# Revit family: RN 57037 Optifitt-Press-Übergang
name_source: partatom
category: Rohrformteile
units: mm (PartAtom-declared; Revit-internal decimal feet)

## family parameters
Arbeitsebenenbasiert = Nein
Beim Laden mit Abzugskörper schneiden = Nein
Bemaßung runder Anschluss = Durchmesser verwenden
Gemeinsam genutzt = Nein
Immer vertikal = Ja
Teiletyp = Verbindung

## types (9) — shared parameters
1.010.00.2 Blattnummer der Richtlinie = 29
1.010.00.3 Ausgabedatum (Monat) der Richtlinie = 201308
1.010.00.4 Herstellername = R. Nussbaum AG
1.010.00.5 Revisionsdatum der Datei = 20190521
1.010.00.6 Webadresse des Herstellers = http://www.nussbaum.ch
1.100.00.4 Produktbezeichnung = Versorgung
1.110.00.2 Index = 2
1.110.00.4 Produktbezeichnung = Optifitt-Press
1.960/3L.00.8 Link (URL) = https://www.nussbaum.ch
29.700.00.4 Produktname = Optifitt-Press-Übergang, auf Optipress-Therm
29.700.00.5 Produktkennung = 2
29.700.00.6 Querschnittsform = 1
29.700.00.7 Nennweitensystem = DN
29.700.00.8 Nenndrucksystem = PN
29.710.02.4 Nenndruck = 16
29.710.02.5 max. zul. Überdruck [hPa] = 1600
29.710.02.7 max. zul. Dauer-Betriebsdruck [hPa] = 1600
29.710.02.9 max. zul. Dauer-Betriebstemperatur [°C] = 95
Beschreibung = Optifitt-Press-Übergang
Connector Visibility = Nein
EnclosingSpace Visibility = Nein
Hersteller = R. Nussbaum AG
URL = https://www.nussbaum.ch

## per-type parameters (varying)
- DN=25: 1.800.00.3 TGA-Nummer=01900200000000000000000000000000000000000000000016000000000000000009; 1.800.00.4 Kommentarfeld=57037.30, Optifitt-Press-Übergang, auf Optipress-Therm, DN=25, L=79; 1.810.00.3 Hersteller-Bestellnummer=57037.30; 1.810.00.4 DATANORM-Nummer=57037.30; 1.810.00.6 GTIN-Nummer=7612945735096; 29.710.02.10 Formstück-Gewicht [kg]=0.175; 29.710.02.3 Benennung=Optifitt-Press-Übergang, auf Optipress-Therm, DN=25, L=79; CONNECTOR0_DIAMETER_dX_0r=25 mm  [stored 0.082021 ft]; CONNECTOR0_dX_01=34 mm; CONNECTOR0_ref_dX=34 mm; CONNECTOR1_DIAMETER_dX_0r=25 mm  [stored 0.082021 ft]; CONNECTOR1_dX_00=57 mm; CONNECTOR1_dX_01=79 mm; CONNECTOR1_ref_dX=57 mm; Modell=57037.3; R. Nussbaum AG 57037.22 de Visibility=Nein; R. Nussbaum AG 57037.23 de Visibility=Nein; R. Nussbaum AG 57037.24 de Visibility=Nein; R. Nussbaum AG 57037.25 de Visibility=Nein; R. Nussbaum AG 57037.26 de Visibility=Nein; R. Nussbaum AG 57037.27 de Visibility=Nein; R. Nussbaum AG 57037.28 de Visibility=Nein; R. Nussbaum AG 57037.29 de Visibility=Nein; R. Nussbaum AG 57037.30 de Visibility=Ja; Typenkommentare=Optifitt-Press-Übergang  DN=25
- DN=20: 1.800.00.3 TGA-Nummer=01900200000000000000000000000000000000000000000016000000000000000008; 1.800.00.4 Kommentarfeld=57037.29, Optifitt-Press-Übergang, auf Optipress-Therm, DN=20, L=73; 1.810.00.3 Hersteller-Bestellnummer=57037.29; 1.810.00.4 DATANORM-Nummer=57037.29; 1.810.00.6 GTIN-Nummer=7612945735089; 29.710.02.10 Formstück-Gewicht [kg]=0.125; 29.710.02.3 Benennung=Optifitt-Press-Übergang, auf Optipress-Therm, DN=20, L=73; CONNECTOR0_DIAMETER_dX_0r=20 mm; CONNECTOR0_dX_01=29 mm; CONNECTOR0_ref_dX=29 mm; CONNECTOR1_DIAMETER_dX_0r=20 mm; CONNECTOR1_dX_00=51 mm; CONNECTOR1_dX_01=73 mm; CONNECTOR1_ref_dX=51 mm; Modell=57037.29; R. Nussbaum AG 57037.22 de Visibility=Nein; R. Nussbaum AG 57037.23 de Visibility=Nein; R. Nussbaum AG 57037.24 de Visibility=Nein; R. Nussbaum AG 57037.25 de Visibility=Nein; R. Nussbaum AG 57037.26 de Visibility=Nein; R. Nussbaum AG 57037.27 de Visibility=Nein; R. Nussbaum AG 57037.28 de Visibility=Nein; R. Nussbaum AG 57037.29 de Visibility=Ja; R. Nussbaum AG 57037.30 de Visibility=Nein; Typenkommentare=Optifitt-Press-Übergang  DN=20
- DN=50: 1.800.00.3 TGA-Nummer=01900200000000000000000000000000000000000000000016000000000000000007; 1.800.00.4 Kommentarfeld=57037.28, Optifitt-Press-Übergang, auf Optipress-Therm, DN=50, L=108; 1.810.00.3 Hersteller-Bestellnummer=57037.28; 1.810.00.4 DATANORM-Nummer=57037.28; 1.810.00.5 StLB-Nummer=255.638; 1.810.00.6 GTIN-Nummer=7612945717832; 29.710.02.10 Formstück-Gewicht [kg]=0.505; 29.710.02.3 Benennung=Optifitt-Press-Übergang, auf Optipress-Therm, DN=50, L=108; CONNECTOR0_DIAMETER_dX_0r=50 mm; CONNECTOR0_dX_01=50 mm; CONNECTOR0_ref_dX=50 mm; CONNECTOR1_DIAMETER_dX_0r=50 mm; CONNECTOR1_dX_00=71 mm; CONNECTOR1_dX_01=111 mm; CONNECTOR1_ref_dX=71 mm; Modell=57037.28; R. Nussbaum AG 57037.22 de Visibility=Nein; R. Nussbaum AG 57037.23 de Visibility=Nein; R. Nussbaum AG 57037.24 de Visibility=Nein; R. Nussbaum AG 57037.25 de Visibility=Nein; R. Nussbaum AG 57037.26 de Visibility=Nein; R. Nussbaum AG 57037.27 de Visibility=Nein; R. Nussbaum AG 57037.28 de Visibility=Ja; R. Nussbaum AG 57037.29 de Visibility=Nein; R. Nussbaum AG 57037.30 de Visibility=Nein; Typenkommentare=Optifitt-Press-Übergang  DN=50
- DN=40: 1.800.00.3 TGA-Nummer=01900200000000000000000000000000000000000000000016000000000000000006; 1.800.00.4 Kommentarfeld=57037.27, Optifitt-Press-Übergang, auf Optipress-Therm, DN=40, L=102; 1.810.00.3 Hersteller-Bestellnummer=57037.27; 1.810.00.4 DATANORM-Nummer=57037.27; 1.810.00.5 StLB-Nummer=255.637; 1.810.00.6 GTIN-Nummer=7612945717825; 29.710.02.10 Formstück-Gewicht [kg]=0.387; 29.710.02.3 Benennung=Optifitt-Press-Übergang, auf Optipress-Therm, DN=40, L=102; CONNECTOR0_DIAMETER_dX_0r=40 mm; CONNECTOR0_dX_01=48 mm; CONNECTOR0_ref_dX=48 mm; CONNECTOR1_DIAMETER_dX_0r=40 mm; CONNECTOR1_dX_00=66 mm; CONNECTOR1_dX_01=102 mm; CONNECTOR1_ref_dX=66 mm; Modell=57037.27; R. Nussbaum AG 57037.22 de Visibility=Nein; R. Nussbaum AG 57037.23 de Visibility=Nein; R. Nussbaum AG 57037.24 de Visibility=Nein; R. Nussbaum AG 57037.25 de Visibility=Nein; R. Nussbaum AG 57037.26 de Visibility=Nein; R. Nussbaum AG 57037.27 de Visibility=Ja; R. Nussbaum AG 57037.28 de Visibility=Nein; R. Nussbaum AG 57037.29 de Visibility=Nein; R. Nussbaum AG 57037.30 de Visibility=Nein; Typenkommentare=Optifitt-Press-Übergang  DN=40
- DN=32: 1.800.00.3 TGA-Nummer=01900200000000000000000000000000000000000000000016000000000000000005; 1.800.00.4 Kommentarfeld=57037.26, Optifitt-Press-Übergang, auf Optipress-Therm, DN=32, L=90; 1.810.00.3 Hersteller-Bestellnummer=57037.26; 1.810.00.4 DATANORM-Nummer=57037.26; 1.810.00.5 StLB-Nummer=255.636; 1.810.00.6 GTIN-Nummer=7612945717818; 29.710.02.10 Formstück-Gewicht [kg]=0.262; 29.710.02.3 Benennung=Optifitt-Press-Übergang, auf Optipress-Therm, DN=32, L=90; CONNECTOR0_DIAMETER_dX_0r=32 mm; CONNECTOR0_dX_01=46 mm; CONNECTOR0_ref_dX=46 mm; CONNECTOR1_DIAMETER_dX_0r=32 mm; CONNECTOR1_dX_00=65 mm; CONNECTOR1_dX_01=91 mm; CONNECTOR1_ref_dX=65 mm; Modell=57037.26; R. Nussbaum AG 57037.22 de Visibility=Nein; R. Nussbaum AG 57037.23 de Visibility=Nein; R. Nussbaum AG 57037.24 de Visibility=Nein; R. Nussbaum AG 57037.25 de Visibility=Nein; R. Nussbaum AG 57037.26 de Visibility=Ja; R. Nussbaum AG 57037.27 de Visibility=Nein; R. Nussbaum AG 57037.28 de Visibility=Nein; R. Nussbaum AG 57037.29 de Visibility=Nein; R. Nussbaum AG 57037.30 de Visibility=Nein; Typenkommentare=Optifitt-Press-Übergang  DN=32
- DN=2: 1.800.00.3 TGA-Nummer=01900200000000000000000000000000000000000000000016000000000000000004; 1.800.00.4 Kommentarfeld=57037.25, Optifitt-Press-Übergang, auf Optipress-Therm, DN=25, L=76; 1.810.00.3 Hersteller-Bestellnummer=57037.25; 1.810.00.4 DATANORM-Nummer=57037.25; 1.810.00.5 StLB-Nummer=255.635; 1.810.00.6 GTIN-Nummer=7612945717801; 29.710.02.10 Formstück-Gewicht [kg]=0.177; 29.710.02.3 Benennung=Optifitt-Press-Übergang, auf Optipress-Therm, DN=25, L=76; CONNECTOR0_DIAMETER_dX_0r=25 mm  [stored 0.082021 ft]; CONNECTOR0_dX_01=34 mm; CONNECTOR0_ref_dX=34 mm; CONNECTOR1_DIAMETER_dX_0r=25 mm  [stored 0.082021 ft]; CONNECTOR1_dX_00=53 mm; CONNECTOR1_dX_01=77 mm; CONNECTOR1_ref_dX=53 mm; Modell=57037.25; R. Nussbaum AG 57037.22 de Visibility=Nein; R. Nussbaum AG 57037.23 de Visibility=Nein; R. Nussbaum AG 57037.24 de Visibility=Nein; R. Nussbaum AG 57037.25 de Visibility=Ja; R. Nussbaum AG 57037.26 de Visibility=Nein; R. Nussbaum AG 57037.27 de Visibility=Nein; R. Nussbaum AG 57037.28 de Visibility=Nein; R. Nussbaum AG 57037.29 de Visibility=Nein; R. Nussbaum AG 57037.30 de Visibility=Nein; Typenkommentare=Optifitt-Press-Übergang  DN=25
- DN=1: 1.800.00.3 TGA-Nummer=01900200000000000000000000000000000000000000000016000000000000000003; 1.800.00.4 Kommentarfeld=57037.24, Optifitt-Press-Übergang, auf Optipress-Therm, DN=20, L=70; 1.810.00.3 Hersteller-Bestellnummer=57037.24; 1.810.00.4 DATANORM-Nummer=57037.24; 1.810.00.5 StLB-Nummer=255.634; 1.810.00.6 GTIN-Nummer=7612945717795; 29.710.02.10 Formstück-Gewicht [kg]=0.118; 29.710.02.3 Benennung=Optifitt-Press-Übergang, auf Optipress-Therm, DN=20, L=70; CONNECTOR0_DIAMETER_dX_0r=20 mm; CONNECTOR0_dX_01=29 mm; CONNECTOR0_ref_dX=29 mm; CONNECTOR1_DIAMETER_dX_0r=20 mm; CONNECTOR1_dX_00=47 mm; CONNECTOR1_dX_01=71 mm; CONNECTOR1_ref_dX=47 mm; Modell=57037.24; R. Nussbaum AG 57037.22 de Visibility=Nein; R. Nussbaum AG 57037.23 de Visibility=Nein; R. Nussbaum AG 57037.24 de Visibility=Ja; R. Nussbaum AG 57037.25 de Visibility=Nein; R. Nussbaum AG 57037.26 de Visibility=Nein; R. Nussbaum AG 57037.27 de Visibility=Nein; R. Nussbaum AG 57037.28 de Visibility=Nein; R. Nussbaum AG 57037.29 de Visibility=Nein; R. Nussbaum AG 57037.30 de Visibility=Nein; Typenkommentare=Optifitt-Press-Übergang  DN=20
- DN=15x12: 1.800.00.3 TGA-Nummer=01900200000000000000000000000000000000000000000016000000000000000002; 1.800.00.4 Kommentarfeld=57037.23, Optifitt-Press-Übergang, auf Optipress-Therm, DN=15x12, L=67; 1.810.00.3 Hersteller-Bestellnummer=57037.23; 1.810.00.4 DATANORM-Nummer=57037.23; 1.810.00.5 StLB-Nummer=255.633; 1.810.00.6 GTIN-Nummer=7612945717788; 29.710.02.10 Formstück-Gewicht [kg]=0.093; 29.710.02.3 Benennung=Optifitt-Press-Übergang, auf Optipress-Therm, DN=15x12, L=67; CONNECTOR0_DIAMETER_dX_0r=15 mm; CONNECTOR0_dX_01=27 mm; CONNECTOR0_ref_dX=27 mm; CONNECTOR1_DIAMETER_dX_0r=12 mm  [stored 0.0393701 ft]; CONNECTOR1_dX_00=46 mm; CONNECTOR1_dX_01=68 mm; CONNECTOR1_ref_dX=46 mm; Modell=57037.23; R. Nussbaum AG 57037.22 de Visibility=Nein; R. Nussbaum AG 57037.23 de Visibility=Ja; R. Nussbaum AG 57037.24 de Visibility=Nein; R. Nussbaum AG 57037.25 de Visibility=Nein; R. Nussbaum AG 57037.26 de Visibility=Nein; R. Nussbaum AG 57037.27 de Visibility=Nein; R. Nussbaum AG 57037.28 de Visibility=Nein; R. Nussbaum AG 57037.29 de Visibility=Nein; R. Nussbaum AG 57037.30 de Visibility=Nein; Typenkommentare=Optifitt-Press-Übergang  DN=15x12
- DN=10: 1.800.00.3 TGA-Nummer=01900200000000000000000000000000000000000000000016000000000000000001; 1.800.00.4 Kommentarfeld=57037.22, Optifitt-Press-Übergang, auf Optipress-Therm, DN=10, L=64; 1.810.00.3 Hersteller-Bestellnummer=57037.22; 1.810.00.4 DATANORM-Nummer=57037.22; 1.810.00.6 GTIN-Nummer=7612945741349; 29.710.02.10 Formstück-Gewicht [kg]=0.064; 29.710.02.3 Benennung=Optifitt-Press-Übergang, auf Optipress-Therm, DN=10, L=64; CONNECTOR0_DIAMETER_dX_0r=10 mm  [stored 0.0328084 ft]; CONNECTOR0_dX_01=24 mm; CONNECTOR0_ref_dX=24 mm; CONNECTOR1_DIAMETER_dX_0r=10 mm  [stored 0.0328084 ft]; CONNECTOR1_dX_00=42 mm; CONNECTOR1_dX_01=64 mm; CONNECTOR1_ref_dX=42 mm; Modell=57037.22; R. Nussbaum AG 57037.22 de Visibility=Ja; R. Nussbaum AG 57037.23 de Visibility=Nein; R. Nussbaum AG 57037.24 de Visibility=Nein; R. Nussbaum AG 57037.25 de Visibility=Nein; R. Nussbaum AG 57037.26 de Visibility=Nein; R. Nussbaum AG 57037.27 de Visibility=Nein; R. Nussbaum AG 57037.28 de Visibility=Nein; R. Nussbaum AG 57037.29 de Visibility=Nein; R. Nussbaum AG 57037.30 de Visibility=Nein; Typenkommentare=Optifitt-Press-Übergang  DN=10

note: [stored X ft] marks values corroborated as IEEE doubles in the binary element streams (Revit-internal decimal feet)

## geometry (parser evidence)
native form markers: Sweep x1
no freeform markers — native parametric forms only
